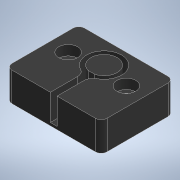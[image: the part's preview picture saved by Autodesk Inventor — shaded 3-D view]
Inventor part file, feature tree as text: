
AUTODESK INVENTOR PART (.ipt)
format: ipt  version: 2022.2 (Build 262287010, 287A)  size: 156,672 bytes
history: native  units: mm
features: sketch x4, extrude x3, fillet x2, hole x1
ambient origin geometry x8: Origin, YZ Plane, XZ Plane, XY Plane, X Axis, Y Axis, Z Axis, Center Point
bodies: Volumenkörper1 (feature_tree)
feature tree (10):
  extrude  "Extrusion1"  Depth=25.0mm
  extrude  "Extrusion2"  Depth=2.3mm
  extrude  "Extrusion3"  Depth=9.0mm TaperAngle=0.0deg
  fillet  "Rundung1"  Radius=9.0mm
  hole  "Bohrung2"  [1 undecoded]
  fillet  "Rundung2"  Radius=3.0mm
  sketch  "Skizze1"  dims[d0=32.7mm d1=25.0mm]
  sketch  "Skizze3"  dims[d2=10.0mm d3=0.0mm d11=2.3mm]
  sketch  "Skizze4"  dims[d12=13.0mm d14=9.0mm d15=0.0mm d16=9.0mm]
  sketch  "Skizze5"  dims[d17=1.5mm d18=8.0mm d19=0.0mm d20=3.0mm d21=10.0mm d22=20.0mm d23=3.4mm d24=6.0mm d25=6.5mm d26=3.4mm d27=90.0deg d28=8.0mm d29=20.594885mm d30=2.0mm]
note: 1 required parameter value undecoded (feature->parameter linkage not recoverable at this tier; creation-order binding heuristic only, values carry confidence <= 0.55)
